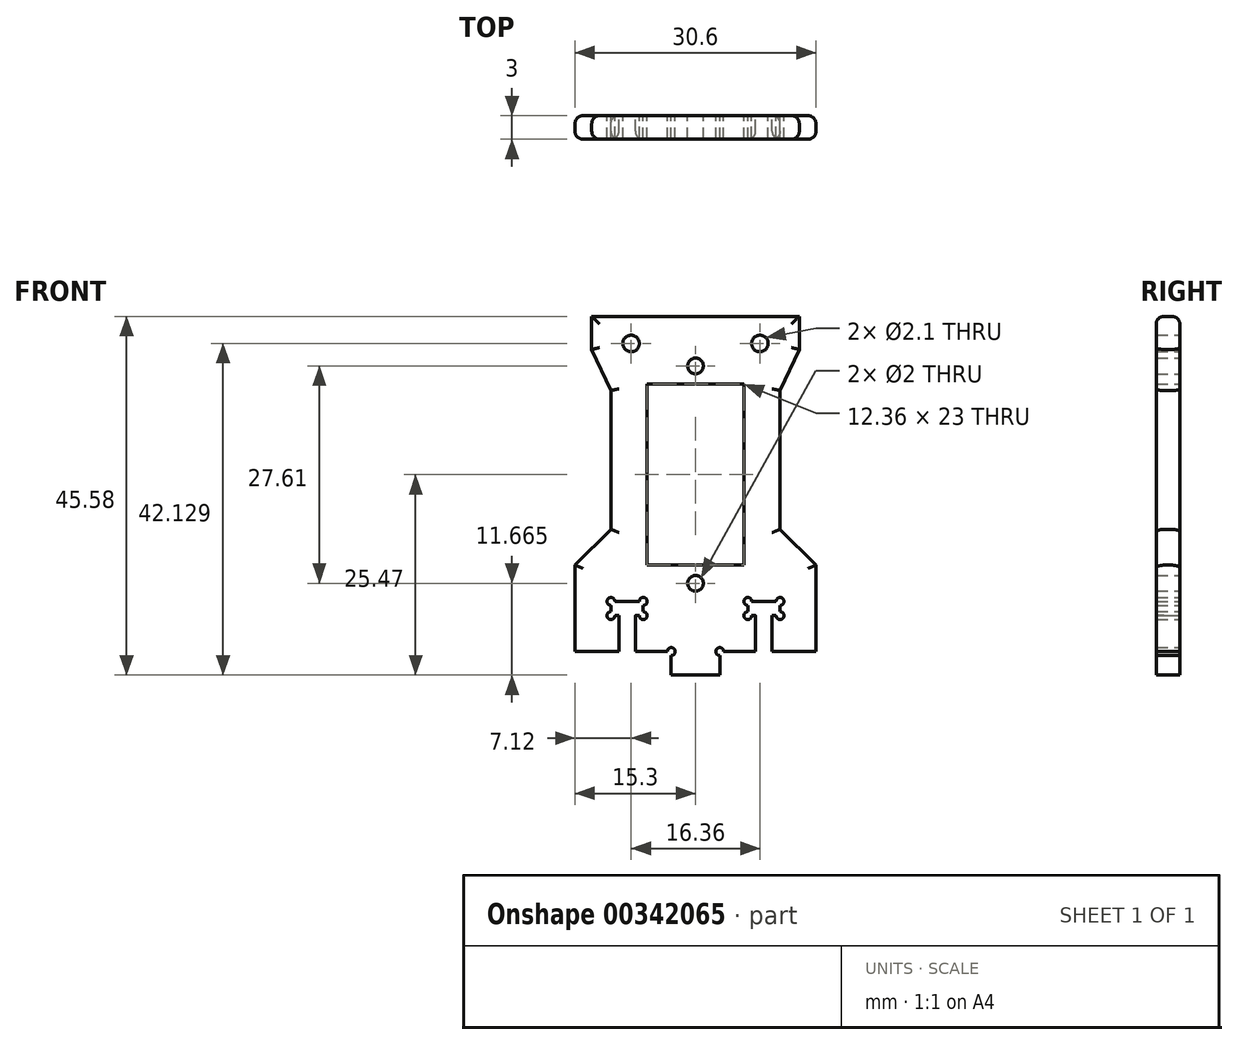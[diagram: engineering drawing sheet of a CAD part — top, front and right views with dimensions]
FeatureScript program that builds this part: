
annotation { "Feature Type Name" : "Feature", "Feature Type Description" : "" }
export const myFeature = defineFeature(function(context is Context, id is Id, definition is map)
    precondition{}
    {
        {
            var Q0;
            Q0=qCreatedBy(makeId("Front.planeOp"),FACE);
            var sketch = newSketch(context, id + "F0", { "sketchPlane" : qUnion([Q0])});
            skLineSegment(sketch, "E0.bottom", {"start": v(10.24, -16.1) * mm, "end": v(7.14, -16.1) * mm});
            skLineSegment(sketch, "E0.left", {"start": v(10.74, -16.1) * mm, "end": v(10.74, 10.68) * mm});
            skLineSegment(sketch, "E0.right", {"start": v(-10.74, -15.6) * mm, "end": v(-10.74, 10.68) * mm});
            skPoint(sketch, "E0.middle", {"position": v(0, 0) * mm});
            skLineSegment(sketch, "E1.bottom", {"start": v(6.18, -11.5) * mm, "end": v(-6.18, -11.5) * mm});
            skLineSegment(sketch, "E1.top", {"start": v(6.18, 11.5) * mm, "end": v(-6.18, 11.5) * mm});
            skLineSegment(sketch, "E1.left", {"start": v(6.18, -11.5) * mm, "end": v(6.18, 11.5) * mm});
            skLineSegment(sketch, "E1.right", {"start": v(-6.18, -11.5) * mm, "end": v(-6.18, 11.5) * mm});
            skCircle(sketch, "E2", {"center": v(0, 13.8) * mm, "radius": 1 * mm});
            skCircle(sketch, "E3", {"center": v(0, -13.8) * mm, "radius": 1 * mm});
            skLineSegment(sketch, "E4", {"start": v(-6.18, -11.5) * mm, "end": v(-6.18, -16.1) * mm});
            skLineSegment(sketch, "E5", {"start": v(6.18, -11.5) * mm, "end": v(6.18, -16.1) * mm});
            skLineSegment(sketch, "E6.bottom", {"start": v(-10.24, -16.1) * mm, "end": v(-7.14, -16.1) * mm});
            skLineSegment(sketch, "E6.top", {"start": v(-10.24, -17.9) * mm, "end": v(-9.74, -17.9) * mm});
            skLineSegment(sketch, "E6.left", {"start": v(-10.74, -16.6) * mm, "end": v(-10.74, -17.4) * mm});
            skLineSegment(sketch, "E6.right", {"start": v(-6.64, -16.6) * mm, "end": v(-6.64, -17.4) * mm});
            skLineSegment(sketch, "E7.top", {"start": v(10.24, -17.9) * mm, "end": v(9.74, -17.9) * mm});
            skLineSegment(sketch, "E7.left", {"start": v(10.74, -16.6) * mm, "end": v(10.74, -17.4) * mm});
            skLineSegment(sketch, "E7.right", {"start": v(6.64, -16.6) * mm, "end": v(6.64, -17.4) * mm});
            skLineSegment(sketch, "E8.bottom", {"start": v(-15.3, -11.5) * mm, "end": v(15.3, -11.5) * mm});
            skLineSegment(sketch, "E8.top", {"start": v(-15.3, -22.47) * mm, "end": v(-9.74, -22.47) * mm});
            skLineSegment(sketch, "E8.left", {"start": v(-15.3, -11.5) * mm, "end": v(-15.3, -22.47) * mm});
            skLineSegment(sketch, "E8.right", {"start": v(15.3, -11.5) * mm, "end": v(15.3, -22.47) * mm});
            skLineSegment(sketch, "E9", {"start": v(-15.3, -11.5) * mm, "end": v(-10.74, -6.94) * mm});
            skLineSegment(sketch, "E10", {"start": v(15.3, -11.5) * mm, "end": v(10.74, -6.94) * mm});
            skLineSegment(sketch, "E11.left", {"start": v(-9.74, -17.91) * mm, "end": v(-9.74, -22.47) * mm});
            skLineSegment(sketch, "E11.right", {"start": v(-7.64, -17.91) * mm, "end": v(-7.64, -22.47) * mm});
            skLineSegment(sketch, "E12.left", {"start": v(7.64, -17.9) * mm, "end": v(7.64, -22.47) * mm});
            skLineSegment(sketch, "E12.right", {"start": v(9.74, -17.9) * mm, "end": v(9.74, -22.47) * mm});
            skPoint(sketch, "E13", {"position": v(-8.7, -17.9) * mm});
            skPoint(sketch, "E14", {"position": v(8.7, -17.9) * mm});
            skLineSegment(sketch, "E15.bottom", {"start": v(-2.58, -22.47) * mm, "end": v(2.58, -22.47) * mm});
            skLineSegment(sketch, "E15.top", {"start": v(-3.08, -25.47) * mm, "end": v(3.08, -25.47) * mm});
            skLineSegment(sketch, "E15.left", {"start": v(-3.08, -22.97) * mm, "end": v(-3.08, -25.47) * mm});
            skLineSegment(sketch, "E15.right", {"start": v(3.08, -22.97) * mm, "end": v(3.08, -25.47) * mm});
            skPoint(sketch, "E16", {"position": v(0, -22.47) * mm});
            skArc(sketch, "E17", {"start": v(-10.74, -17.4) * mm, "mid": v(-11.1, -18.26) * mm, "end": v(-10.24, -17.9) * mm});
            skArc(sketch, "E18", {"start": v(-10.24, -16.1) * mm, "mid": v(-11.1, -15.76) * mm, "end": v(-10.74, -16.6) * mm});
            skArc(sketch, "E19", {"start": v(-6.64, -16.6) * mm, "mid": v(-6.29, -15.76) * mm, "end": v(-7.14, -16.1) * mm});
            skArc(sketch, "E20", {"start": v(-7.14, -17.9) * mm, "mid": v(-6.29, -18.26) * mm, "end": v(-6.64, -17.4) * mm});
            skArc(sketch, "E21", {"start": v(7.14, -16.1) * mm, "mid": v(6.29, -15.76) * mm, "end": v(6.64, -16.6) * mm});
            skArc(sketch, "E22", {"start": v(6.64, -17.4) * mm, "mid": v(6.29, -18.26) * mm, "end": v(7.14, -17.9) * mm});
            skArc(sketch, "E23", {"start": v(10.74, -16.6) * mm, "mid": v(11.1, -15.76) * mm, "end": v(10.24, -16.1) * mm});
            skArc(sketch, "E24", {"start": v(10.24, -17.9) * mm, "mid": v(11.1, -18.26) * mm, "end": v(10.74, -17.4) * mm});
            skArc(sketch, "E25", {"start": v(3.58, -22.47) * mm, "mid": v(2.73, -22.12) * mm, "end": v(3.08, -22.97) * mm});
            skArc(sketch, "E26", {"start": v(-3.08, -22.97) * mm, "mid": v(-2.73, -22.12) * mm, "end": v(-3.58, -22.47) * mm});
            skLineSegment(sketch, "E27.trimOffspring", {"start": v(-7.14, -16.1) * mm, "end": v(-10.24, -16.1) * mm});
            skLineSegment(sketch, "E28.trimOffspring", {"start": v(3.58, -22.47) * mm, "end": v(7.64, -22.47) * mm});
            skLineSegment(sketch, "E29.trimOffspring", {"start": v(7.64, -17.9) * mm, "end": v(7.14, -17.9) * mm});
            skLineSegment(sketch, "E30.trimOffspring", {"start": v(6.18, -16.1) * mm, "end": v(-6.18, -16.1) * mm});
            skLineSegment(sketch, "E31.trimOffspring", {"start": v(9.74, -22.47) * mm, "end": v(15.3, -22.47) * mm});
            skLineSegment(sketch, "E32.trimOffspring", {"start": v(-7.64, -17.9) * mm, "end": v(-7.14, -17.9) * mm});
            skLineSegment(sketch, "E33.trimOffspring", {"start": v(-7.64, -22.47) * mm, "end": v(-3.58, -22.47) * mm});
            skCircle(sketch, "E34", {"center": v(-8.18, 16.66) * mm, "radius": 1.05 * mm});
            skCircle(sketch, "E35", {"center": v(8.18, 16.66) * mm, "radius": 1.05 * mm});
            skLineSegment(sketch, "E36", {"start": v(10.74, 10.68) * mm, "end": v(13.18, 15.9) * mm});
            skLineSegment(sketch, "E37", {"start": v(-10.74, 10.68) * mm, "end": v(-13.18, 15.9) * mm});
            skLineSegment(sketch, "E38", {"start": v(-13.18, 15.9) * mm, "end": v(-13.18, 20.1) * mm});
            skLineSegment(sketch, "E39", {"start": v(-13.18, 20.1) * mm, "end": v(13.18, 20.1) * mm});
            skLineSegment(sketch, "E40", {"start": v(13.18, 20.1) * mm, "end": v(13.18, 15.9) * mm});
            skCircle(sketch, "E41", {"center": v(0, 5.32) * mm, "radius": 6.18 * mm, "construction": true});
            skPoint(sketch, "E41.centerSnap0", {"position": v(0, 11.5) * mm});
            skLineSegment(sketch, "E42", {"start": v(-6.18, -16.1) * mm, "end": v(6.18, -11.5) * mm, "construction": true});
            skLineSegment(sketch, "E43", {"start": v(6.18, -16.1) * mm, "end": v(-6.18, -11.5) * mm, "construction": true});
            skLineSegment(sketch, "E44.bottom", {"start": v(6.18, 11.5) * mm, "end": v(-6.18, 11.5) * mm, "construction": true});
            skLineSegment(sketch, "E44.top", {"start": v(6.18, 16.1) * mm, "end": v(-6.18, 16.1) * mm, "construction": true});
            skLineSegment(sketch, "E44.left", {"start": v(6.18, 11.5) * mm, "end": v(6.18, 16.1) * mm, "construction": true});
            skLineSegment(sketch, "E44.right", {"start": v(-6.18, 11.5) * mm, "end": v(-6.18, 16.1) * mm, "construction": true});
            skLineSegment(sketch, "E45", {"start": v(-6.18, 11.5) * mm, "end": v(6.18, 16.1) * mm, "construction": true});
            skLineSegment(sketch, "E46", {"start": v(6.18, 11.5) * mm, "end": v(-6.18, 16.1) * mm, "construction": true});
            skSolve(sketch);
        }
        {
            var Q0;
            Q0=makeQuery(id+"F0.imprint","IMPRINT",FACE,{"disambiguationData":[TD([[makeQuery(id+"F0.imprint","IMPRINT",EDGE,{"derivedFrom":sQuery(id+"F0.wireOp",EDGE,"E15.bottom")}),-1.0]])]});
            var Q1;
            {var subQ0=sQuery(id+"F0.wireOp",EDGE,"E10");Q1=makeQuery(id+"F0.imprint","IMPRINT",FACE,{"disambiguationData":[TD([[makeQuery(id+"F0.imprint","IMPRINT",EDGE,{"derivedFrom":subQ0}),1.0]])]});}
            var Q2;
            {var subQ0=sQuery(id+"F0.wireOp",EDGE,"E9");Q2=makeQuery(id+"F0.imprint","IMPRINT",FACE,{"disambiguationData":[TD([[makeQuery(id+"F0.imprint","IMPRINT",EDGE,{"derivedFrom":subQ0}),-1.0]])]});}
            var Q3;
            Q3=makeQuery(id+"F0.imprint","IMPRINT",FACE,{"disambiguationData":[TD([[makeQuery(id+"F0.imprint","IMPRINT",EDGE,{"derivedFrom":sQuery(id+"F0.wireOp",EDGE,"ZplLBCht-MEbq-9qZc-Yp2g-QLO0PEXXqDaA.top")}),-1.0]])]});
            var Q4;
            {var subQ5=sQuery(id+"F0.wireOp",EDGE,"E7.left");Q4=makeQuery(id+"F0.imprint","IMPRINT",FACE,{"disambiguationData":[TD([[makeQuery(id+"F0.imprint","IMPRINT",EDGE,{"derivedFrom":subQ5}),1.0]])]});}
            var Q5;
            {var subQ4=sQuery(id+"F0.wireOp",EDGE,"E6.left");Q5=makeQuery(id+"F0.imprint","IMPRINT",FACE,{"disambiguationData":[TD([[makeQuery(id+"F0.imprint","IMPRINT",EDGE,{"derivedFrom":subQ4}),-1.0]])]});}
            var Q6;
            {var subQ5=sQuery(id+"F0.wireOp",EDGE,"E1.left");Q6=makeQuery(id+"F0.imprint","IMPRINT",FACE,{"disambiguationData":[TD([[makeQuery(id+"F0.imprint","IMPRINT",EDGE,{"derivedFrom":subQ5}),-1.0]])]});}
            var Q7;
            {var subQ1=sQuery(id+"F0.wireOp",EDGE,"E1.right");Q7=makeQuery(id+"F0.imprint","IMPRINT",FACE,{"disambiguationData":[TD([[makeQuery(id+"F0.imprint","IMPRINT",EDGE,{"derivedFrom":subQ1}),1.0]])]});}
            var Q8;
            {var subQ4=sQuery(id+"F0.wireOp",EDGE,"E6.right");Q8=makeQuery(id+"F0.imprint","IMPRINT",FACE,{"disambiguationData":[TD([[makeQuery(id+"F0.imprint","IMPRINT",EDGE,{"derivedFrom":subQ4}),1.0]])]});}
            var Q9;
            Q9=makeQuery(id+"F0.imprint","IMPRINT",FACE,{"disambiguationData":[TD([[makeQuery(id+"F0.imprint","IMPRINT",EDGE,{"derivedFrom":sQuery(id+"F0.wireOp",EDGE,"E1.top")}),-1.0]])]});
            var Q10;
            Q10=makeQuery(id+"F0.imprint","IMPRINT",FACE,{"disambiguationData":[TD([[makeQuery(id+"F0.imprint","IMPRINT",EDGE,{"derivedFrom":sQuery(id+"F0.wireOp",EDGE,"E3")}),-1.0]])]});
            var Q11;
            {var subQ2=sQuery(id+"F0.wireOp",EDGE,"E4");Q11=makeQuery(id+"F0.imprint","IMPRINT",FACE,{"disambiguationData":[TD([[makeQuery(id+"F0.imprint","IMPRINT",EDGE,{"derivedFrom":subQ2}),-1.0]])]});}
            var Q12;
            {var subQ0=sQuery(id+"F0.wireOp",EDGE,"E5");Q12=makeQuery(id+"F0.imprint","IMPRINT",FACE,{"disambiguationData":[TD([[makeQuery(id+"F0.imprint","IMPRINT",EDGE,{"derivedFrom":subQ0}),1.0]])]});}
            var Q13;
            Q13=makeQuery(id+"F0.imprint","IMPRINT",FACE,{"disambiguationData":[TD([[makeQuery(id+"F0.imprint","IMPRINT",EDGE,{"derivedFrom":sQuery(id+"F0.wireOp",EDGE,"E15.top")}),1.0]])]});
            extrude(context, id + "F1", {"entities" : qUnion([Q0, Q1, Q2, Q3, Q4, Q5, Q6, Q7, Q8, Q9, Q10, Q11, Q12, Q13]), "depth" : 3 * mm});
        }
        {
            var Q0;
            Q0=makeQuery(id+"F1.opExtrude","CAP_EDGE",EDGE,{"disambiguationData":[OSD([sQuery(id+"F0.wireOp",EDGE,"E39")])],"isStart":false});
            var Q1;
            Q1=makeQuery(id+"F1.opExtrude","CAP_EDGE",EDGE,{"disambiguationData":[OSD([sQuery(id+"F0.wireOp",EDGE,"E38")])],"isStart":false});
            var Q2;
            Q2=makeQuery(id+"F1.opExtrude","CAP_EDGE",EDGE,{"disambiguationData":[OSD([sQuery(id+"F0.wireOp",EDGE,"E37")])],"isStart":false});
            var Q3;
            Q3=makeQuery(id+"F1.opExtrude","CAP_EDGE",EDGE,{"disambiguationData":[OSD([sQuery(id+"F0.wireOp",EDGE,"E0.right")])],"isStart":false});
            var Q4;
            Q4=makeQuery(id+"F1.opExtrude","CAP_EDGE",EDGE,{"disambiguationData":[OSD([sQuery(id+"F0.wireOp",EDGE,"E9")])],"isStart":false});
            var Q5;
            Q5=makeQuery(id+"F1.opExtrude","CAP_EDGE",EDGE,{"disambiguationData":[OSD([sQuery(id+"F0.wireOp",EDGE,"E8.left")])],"isStart":false});
            var Q6;
            Q6=makeQuery(id+"F1.opExtrude","CAP_EDGE",EDGE,{"disambiguationData":[OSD([sQuery(id+"F0.wireOp",EDGE,"E8.right")])],"isStart":false});
            var Q7;
            Q7=makeQuery(id+"F1.opExtrude","CAP_EDGE",EDGE,{"disambiguationData":[OSD([sQuery(id+"F0.wireOp",EDGE,"E10")])],"isStart":false});
            var Q8;
            Q8=makeQuery(id+"F1.opExtrude","CAP_EDGE",EDGE,{"disambiguationData":[OSD([sQuery(id+"F0.wireOp",EDGE,"E0.left")])],"isStart":false});
            var Q9;
            Q9=makeQuery(id+"F1.opExtrude","CAP_EDGE",EDGE,{"disambiguationData":[OSD([sQuery(id+"F0.wireOp",EDGE,"E36")])],"isStart":false});
            var Q10;
            Q10=makeQuery(id+"F1.opExtrude","CAP_EDGE",EDGE,{"disambiguationData":[OSD([sQuery(id+"F0.wireOp",EDGE,"E40")])],"isStart":false});
            var Q11;
            Q11=makeQuery(id+"F1.opExtrude","CAP_EDGE",EDGE,{"disambiguationData":[OSD([sQuery(id+"F0.wireOp",EDGE,"E12.left")])],"isStart":false});
            var Q12;
            Q12=makeQuery(id+"F1.opExtrude","CAP_EDGE",EDGE,{"disambiguationData":[OSD([sQuery(id+"F0.wireOp",EDGE,"E12.right")])],"isStart":false});
            var Q13;
            Q13=makeQuery(id+"F1.opExtrude","CAP_EDGE",EDGE,{"disambiguationData":[OSD([sQuery(id+"F0.wireOp",EDGE,"E11.right")])],"isStart":false});
            var Q14;
            Q14=makeQuery(id+"F1.opExtrude","CAP_EDGE",EDGE,{"disambiguationData":[OSD([sQuery(id+"F0.wireOp",EDGE,"E11.left")])],"isStart":false});
            var Q15;
            Q15=makeQuery(id+"F1.opExtrude","CAP_EDGE",EDGE,{"disambiguationData":[OSD([sQuery(id+"F0.wireOp",EDGE,"E39")])],"isStart":true});
            var Q16;
            Q16=makeQuery(id+"F1.opExtrude","CAP_EDGE",EDGE,{"disambiguationData":[OSD([sQuery(id+"F0.wireOp",EDGE,"E40")])],"isStart":true});
            var Q17;
            Q17=makeQuery(id+"F1.opExtrude","CAP_EDGE",EDGE,{"disambiguationData":[OSD([sQuery(id+"F0.wireOp",EDGE,"E36")])],"isStart":true});
            var Q18;
            Q18=makeQuery(id+"F1.opExtrude","CAP_EDGE",EDGE,{"disambiguationData":[OSD([sQuery(id+"F0.wireOp",EDGE,"E38")])],"isStart":true});
            var Q19;
            Q19=makeQuery(id+"F1.opExtrude","CAP_EDGE",EDGE,{"disambiguationData":[OSD([sQuery(id+"F0.wireOp",EDGE,"E37")])],"isStart":true});
            var Q20;
            Q20=makeQuery(id+"F1.opExtrude","CAP_EDGE",EDGE,{"disambiguationData":[OSD([sQuery(id+"F0.wireOp",EDGE,"E0.right")])],"isStart":true});
            var Q21;
            Q21=makeQuery(id+"F1.opExtrude","CAP_EDGE",EDGE,{"disambiguationData":[OSD([sQuery(id+"F0.wireOp",EDGE,"E9")])],"isStart":true});
            var Q22;
            Q22=makeQuery(id+"F1.opExtrude","CAP_EDGE",EDGE,{"disambiguationData":[OSD([sQuery(id+"F0.wireOp",EDGE,"E8.left")])],"isStart":true});
            var Q23;
            Q23=makeQuery(id+"F1.opExtrude","CAP_EDGE",EDGE,{"disambiguationData":[OSD([sQuery(id+"F0.wireOp",EDGE,"E8.right")])],"isStart":true});
            var Q24;
            Q24=makeQuery(id+"F1.opExtrude","CAP_EDGE",EDGE,{"disambiguationData":[OSD([sQuery(id+"F0.wireOp",EDGE,"E10")])],"isStart":true});
            var Q25;
            Q25=makeQuery(id+"F1.opExtrude","CAP_EDGE",EDGE,{"disambiguationData":[OSD([sQuery(id+"F0.wireOp",EDGE,"E0.left")])],"isStart":true});
            fillet(context, id + "F2", {"entities" : qUnion([Q0, Q1, Q2, Q3, Q4, Q5, Q6, Q7, Q8, Q9, Q10, Q11, Q12, Q13, Q14, Q15, Q16, Q17, Q18, Q19, Q20, Q21, Q22, Q23, Q24, Q25]), "radius" : 1 * mm, "tangentPropagation" : true, "allowEdgeOverflow" : false});
        }
    });
